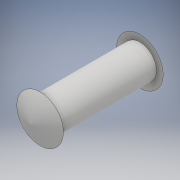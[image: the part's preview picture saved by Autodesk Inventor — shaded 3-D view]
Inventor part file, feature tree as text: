
AUTODESK INVENTOR PART (.ipt)
format: ipt  version: 2018 (Build 220112000, 112)  size: 129,024 bytes
history: native  units: mm
features: sketch x3, extrude x1, revolve x1, plane x1, mirror x1
ambient origin geometry x8: Origin, YZ Plane, XZ Plane, XY Plane, X Axis, Y Axis, Z Axis, Center Point
bodies: Solid1 (feature_tree)
feature tree (7):
  extrude  "Extrusion1"  Depth=30.0mm TaperAngle=0.0deg
  sketch  "Sketch2"  dims[d7=3.0mm d8=7.0mm]
  revolve  "Revolution2"  [1 undecoded]
  plane  "Work Plane2"
  mirror  "Mirror2"
  sketch  "Sketch1"  dims[d0=10.0mm d1=30.0mm d2=0.0mm]
  sketch  "Sketch4"  dims[d9=90.0deg d10=-15.0mm]
note: 1 required parameter value undecoded (feature->parameter linkage not recoverable at this tier; creation-order binding heuristic only, values carry confidence <= 0.55)
